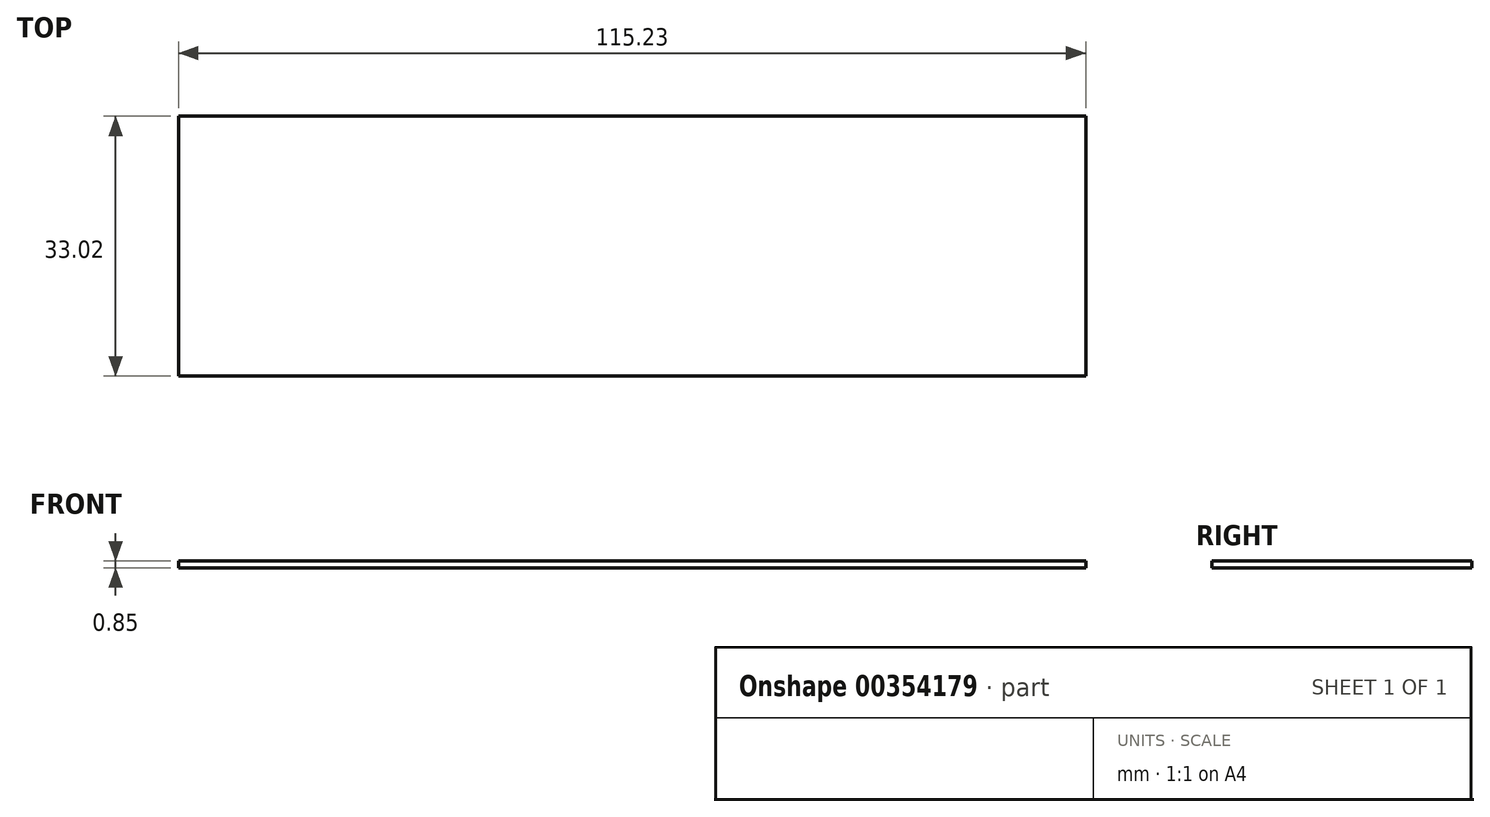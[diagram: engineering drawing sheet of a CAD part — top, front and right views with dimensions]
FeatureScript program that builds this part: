
annotation { "Feature Type Name" : "Feature", "Feature Type Description" : "" }
export const myFeature = defineFeature(function(context is Context, id is Id, definition is map)
    precondition{}
    {
        {
            var Q0;
            Q0=qCreatedBy(makeId("Front.planeOp"),FACE);
            var sketch = newSketch(context, id + "F0", { "sketchPlane" : qUnion([Q0])});
            skLineSegment(sketch, "E0.bottom", {"start": v(-56.2, 29.8) * mm, "end": v(59.04, 29.8) * mm});
            skLineSegment(sketch, "E0.top", {"start": v(-56.2, 30.66) * mm, "end": v(59.04, 30.66) * mm});
            skLineSegment(sketch, "E0.left", {"start": v(-56.2, 29.8) * mm, "end": v(-56.2, 30.66) * mm});
            skLineSegment(sketch, "E0.right", {"start": v(59.04, 29.8) * mm, "end": v(59.04, 30.66) * mm});
            skSolve(sketch);
        }
        {
            var Q0;
            Q0 = qSketchRegion(id + "F0", true);
            extrude(context, id + "F1", {"entities" : qUnion([Q0]), "depth" : 33.02 * mm});
        }
    });
